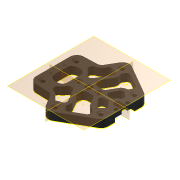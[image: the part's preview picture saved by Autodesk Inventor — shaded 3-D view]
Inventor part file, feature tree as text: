
AUTODESK INVENTOR PART (.ipt)
format: ipt  version: 2016 (Build 200138000, 138)  size: 891,392 bytes
history: native  units: mm
features: sketch x17, extrude x15, plane x3, pattern_circular x3, projected_geometry x3, thread x2, reference x2, chamfer x1, revolve x1, fillet x1
ambient origin geometry x8: Origin, YZ Plane, XZ Plane, XY Plane, X Axis, Y Axis, Z Axis, Center Point
bodies: Solid1 (feature_tree)
feature tree (48):
  extrude  "Extrusion1"  Depth=10.0mm
  extrude  "Extrusion2"  Depth=10.0mm
  extrude  "Extrusion4"  Depth=10.0mm
  chamfer  "Chamfer1"  Distance=8.0mm
  plane  "Work Plane2"
  extrude  "Extrusion10"  Depth=8.0mm TaperAngle=0.0deg
  plane  "Work Plane8"
  extrude  "Extrusion17"  Depth=4.0mm
  extrude  "Extrusion21"  Depth=4.0mm
  extrude  "Extrusion27"  Depth=4.0mm
  extrude  "Extrusion28"  Depth=3.0mm
  extrude  "Extrusion29"  Depth=2.0mm
  plane  "Work Plane10"
  revolve  "Revolution2"  [1 undecoded]
  pattern_circular  "Circular Pattern3"  [2 undecoded]
  thread  "Thread3"  [1 undecoded]
  thread  "Thread4"  [1 undecoded]
  extrude  "Extrusion31"  Depth=4.0mm
  extrude  "Extrusion33"  Depth=10.0mm TaperAngle=0.0deg
  extrude  "Extrusion34"  Depth=8.0mm
  extrude  "Extrusion35"  Depth=8.0mm
  fillet  "Fillet8"  Radius=4.0mm
  extrude  "Extrusion36"  Depth=0.05mm
  extrude  "Extrusion37"  Depth=0.05mm
  pattern_circular  "Circular Pattern6"  [2 undecoded]
  pattern_circular  "Circular Pattern7"  [2 undecoded]
  sketch  "Sketch47"  dims[d133=6.0mm d134=7.5mm d135=8.0mm d136=0.0mm d175=4.0mm d176=4.0mm d177=10.0mm d178=0.0mm d179=8.0mm d180=8.0mm d181=4.0mm d182=0.0mm d183=2.4mm d184=2.4mm d185=8.0mm d186=0.0mm d205=3.5mm d206=10.0mm d207=90.0deg d208=60.0mm d209=360.0deg d211=10.0mm d212=0.0mm d213=10.0mm d214=0.0mm d215=6.0mm d216=6.0mm d217=1.0mm d218=0.0mm d232=8.0mm d233=0.0mm d234=0.349066mm d235=0.349066mm d236=60.0deg d237=60.0deg d238=5.0mm d239=8.0mm d240=0.0mm d243=5.0mm d244=6.0mm d247=3.5mm d248=3.5mm d249=8.0mm d250=8.0mm d251=8.0mm d252=14.0mm d253=8.0mm d254=3.5mm d255=1.75mm d256=6.0mm d260=3.5mm d261=3.5mm d262=3.5mm d263=6.0mm d264=6.0mm d265=6.0mm d266=6.0mm d267=10.0mm d268=10.0mm d269=17.5mm d270=17.5mm d271=3.5mm d272=3.5mm d273=6.0mm d274=6.0mm d275=6.0mm d276=6.0mm d277=3.0mm d279=8.0mm d280=0.0mm d281=3.0mm d282=3.0mm d283=3.0mm d284=0.9mm d285=0.9mm d286=3.6mm d287=3.6mm d288=10.0mm d289=0.0mm d290=10.0mm d291=0.0mm d292=30.0mm d293=360.0deg d295=60.0mm d296=360.0deg d298=0.05mm]
  sketch  "Sketch1"  dims[d1=10.0mm d2=10.0mm]
  reference  "Reference1"
  sketch  "Sketch2"  dims[d3=10.0mm d4=10.0mm]
  reference  "Reference4"
  sketch  "Sketch4"  dims[d5=10.0mm d6=10.0mm d9=8.0mm d10=0.0mm]
  sketch  "Sketch14"  dims[d14=6.5mm d15=8.0mm d16=0.0mm]
  sketch  "Sketch21"  dims[d19=4.0mm d20=4.0mm]
  sketch  "Sketch26"  dims[d21=4.0mm d22=4.0mm]
  sketch  "Sketch34"  dims[d23=4.0mm d24=4.0mm]
  sketch  "Sketch35"  dims[d25=1.5mm d26=0.0mm d31=3.0mm d35=2.2mm d36=2.0mm d37=12.217305mm]
  sketch  "Sketch36"  dims[d55=2.0mm d56=2.0mm]
  sketch  "Sketch38"  dims[d57=2.0mm d58=2.0mm]
  sketch  "Sketch39"  dims[d59=2.0mm]
  sketch  "Sketch41"  dims[d60=2.0mm]
  sketch  "Sketch42"  dims[d61=34.0mm]
  sketch  "Sketch43"  dims[d64=8.2mm]
  sketch  "Sketch45"  dims[d65=5.0mm d66=0.0mm]
  projected_geometry  "Projected Loop2"
  sketch  "Sketch46"  dims[d107=8.0mm d108=0.0mm]
  projected_geometry  "Projected Loop3"
  projected_geometry  "Projected Loop4"
note: 9 required parameter values undecoded (feature->parameter linkage not recoverable at this tier; creation-order binding heuristic only, values carry confidence <= 0.55)